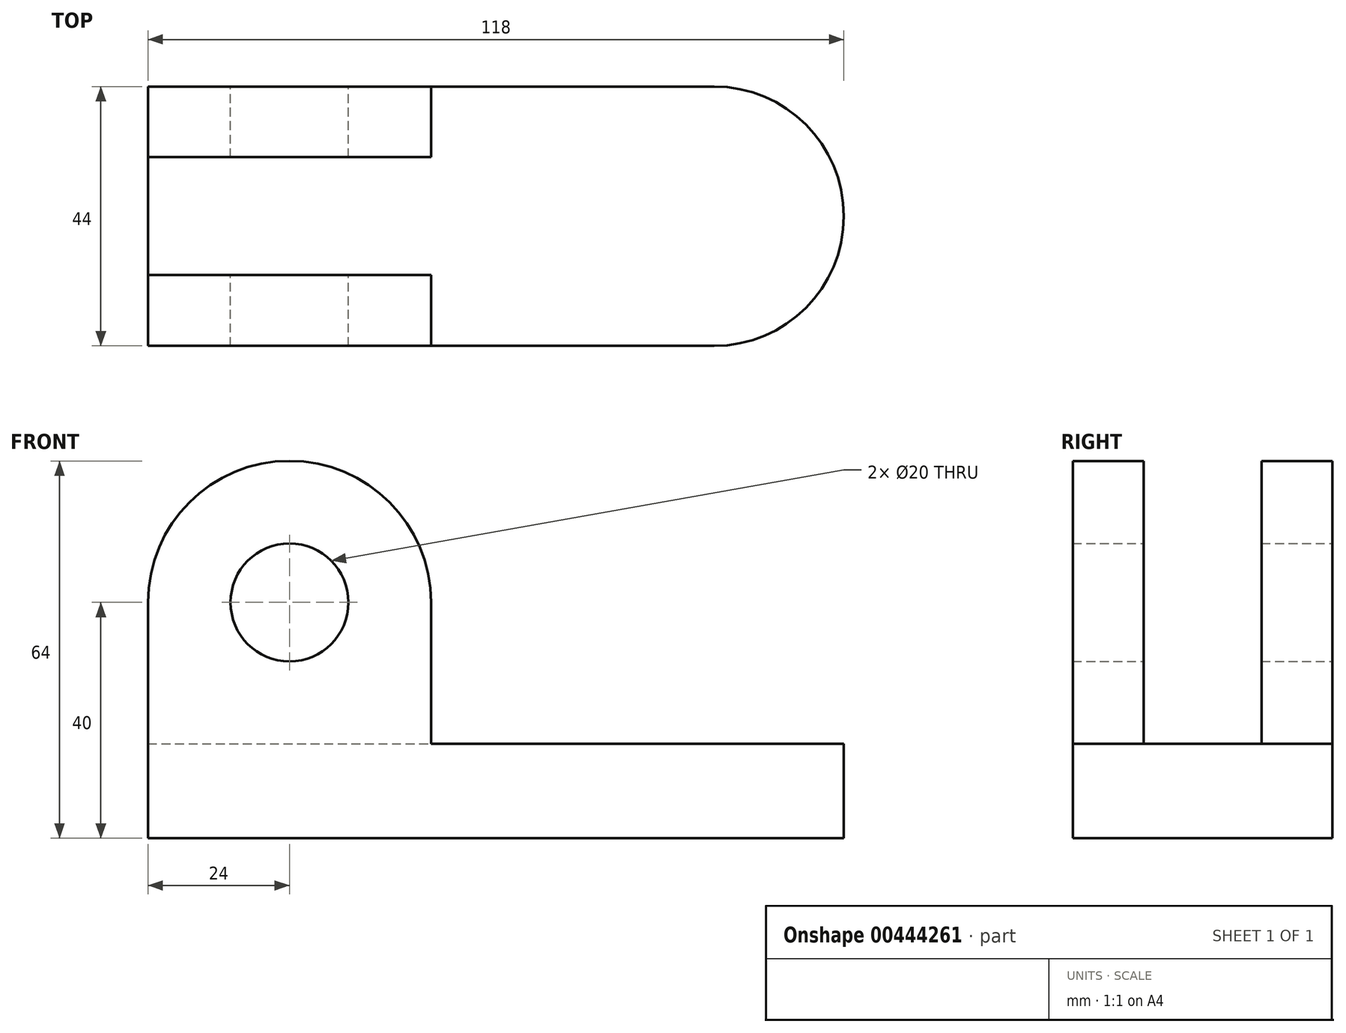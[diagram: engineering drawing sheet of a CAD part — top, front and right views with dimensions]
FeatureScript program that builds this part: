
annotation { "Feature Type Name" : "Feature", "Feature Type Description" : "" }
export const myFeature = defineFeature(function(context is Context, id is Id, definition is map)
    precondition{}
    {
        {
            var Q0;
            Q0=qCreatedBy(makeId("Front.planeOp"),FACE);
            var sketch = newSketch(context, id + "F0", { "sketchPlane" : qUnion([Q0])});
            skCircle(sketch, "E0", {"center": v(0, 0) * mm, "radius": 10 * mm});
            skCircle(sketch, "E1", {"center": v(0, 0) * mm, "radius": 24 * mm});
            skLineSegment(sketch, "E2.bottom", {"start": v(-24, 0) * mm, "end": v(24, 0) * mm});
            skLineSegment(sketch, "E2.top", {"start": v(-24, -40) * mm, "end": v(24, -40) * mm});
            skLineSegment(sketch, "E2.left", {"start": v(-24, 0) * mm, "end": v(-24, -40) * mm});
            skLineSegment(sketch, "E2.right", {"start": v(24, 0) * mm, "end": v(24, -40) * mm});
            skLineSegment(sketch, "E3.bottom", {"start": v(-24, -40) * mm, "end": v(94, -40) * mm});
            skLineSegment(sketch, "E3.top", {"start": v(-24, -24) * mm, "end": v(94, -24) * mm});
            skLineSegment(sketch, "E3.left", {"start": v(-24, -40) * mm, "end": v(-24, -24) * mm});
            skLineSegment(sketch, "E3.right", {"start": v(94, -40) * mm, "end": v(94, -24) * mm});
            skSolve(sketch);
        }
        {
            var Q0;
            Q0 = qSketchRegion(id + "F0", true);
            extrude(context, id + "F1", {"entities" : qUnion([Q0]), "depth" : 22 * mm, "hasSecondDirection" : true, "secondDirectionOppositeDirection" : true, "secondDirectionDepth" : 22 * mm});
        }
        {
            var Q0;
            {var subQ0=sQuery(id+"F0.wireOp",EDGE,"E2.bottom");var subQ3=sQuery(id+"F0.wireOp",EDGE,"E0");var subQ4=makeQuery(id+"F0.imprint","INTERSECT",VERTEX,{"disambiguationData":[OD(0.0)],"derivedFrom":[subQ3,subQ0]});Q0=makeQuery(id+"F0.imprint","IMPRINT",FACE,{"disambiguationData":[TD([[makeQuery(id+"F0.imprint","IMPRINT",EDGE,{"disambiguationData":[TD([[subQ4,-1.0]])],"derivedFrom":subQ3}),-1.0]])]});}
            var Q1;
            {var subQ0=sQuery(id+"F0.wireOp",EDGE,"E2.right");var subQ3=sQuery(id+"F0.wireOp",EDGE,"E3.top");var subQ5=makeQuery(id+"F0.imprint","INTERSECT",VERTEX,{"derivedFrom":[subQ0,subQ3]});Q1=makeQuery(id+"F0.imprint","IMPRINT",FACE,{"disambiguationData":[TD([[makeQuery(id+"F0.imprint","IMPRINT",EDGE,{"disambiguationData":[TD([[subQ5,1.0]])],"derivedFrom":subQ3}),1.0]])]});}
            var Q2;
            {var subQ0=sQuery(id+"F0.wireOp",EDGE,"E2.left");Q2=makeQuery(id+"F0.imprint","IMPRINT",FACE,{"disambiguationData":[TD([[makeQuery(id+"F0.imprint","IMPRINT",EDGE,{"derivedFrom":subQ0}),1.0]])]});}
            var Q3;
            {var subQ0=sQuery(id+"F0.wireOp",EDGE,"E2.bottom");var subQ1=sQuery(id+"F0.wireOp",EDGE,"E0");var subQ2=makeQuery(id+"F0.imprint","INTERSECT",VERTEX,{"disambiguationData":[OD(0.0)],"derivedFrom":[subQ1,subQ0]});Q3=makeQuery(id+"F0.imprint","IMPRINT",FACE,{"disambiguationData":[TD([[makeQuery(id+"F0.imprint","IMPRINT",EDGE,{"disambiguationData":[TD([[subQ2,1.0]])],"derivedFrom":subQ1}),-1.0]])]});}
            extrude(context, id + "F2", {"entities" : qUnion([Q0, Q1, Q2, Q3]), "operationType" : NewBodyOperationType.REMOVE, "oppositeDirection" : true, "depth" : (44 / 2 - 12) * mm, "hasSecondDirection" : true, "secondDirectionOppositeDirection" : false, "secondDirectionDepth" : (44 / 2 - 12) * mm});
        }
        {
            var Q0;
            Q0=makeQuery(id+"F1.opExtrude","CAP_EDGE",EDGE,{"disambiguationData":[OSD([sQuery(id+"F0.wireOp",EDGE,"E3.right")])],"isStart":false});
            var Q1;
            Q1=makeQuery(id+"F1.opExtrude","CAP_EDGE",EDGE,{"disambiguationData":[OSD([sQuery(id+"F0.wireOp",EDGE,"E3.right")])],"isStart":true});
            fillet(context, id + "F3", {"entities" : qUnion([Q0, Q1]), "radius" : 22 * mm, "tangentPropagation" : true, "allowEdgeOverflow" : false});
        }
    });
